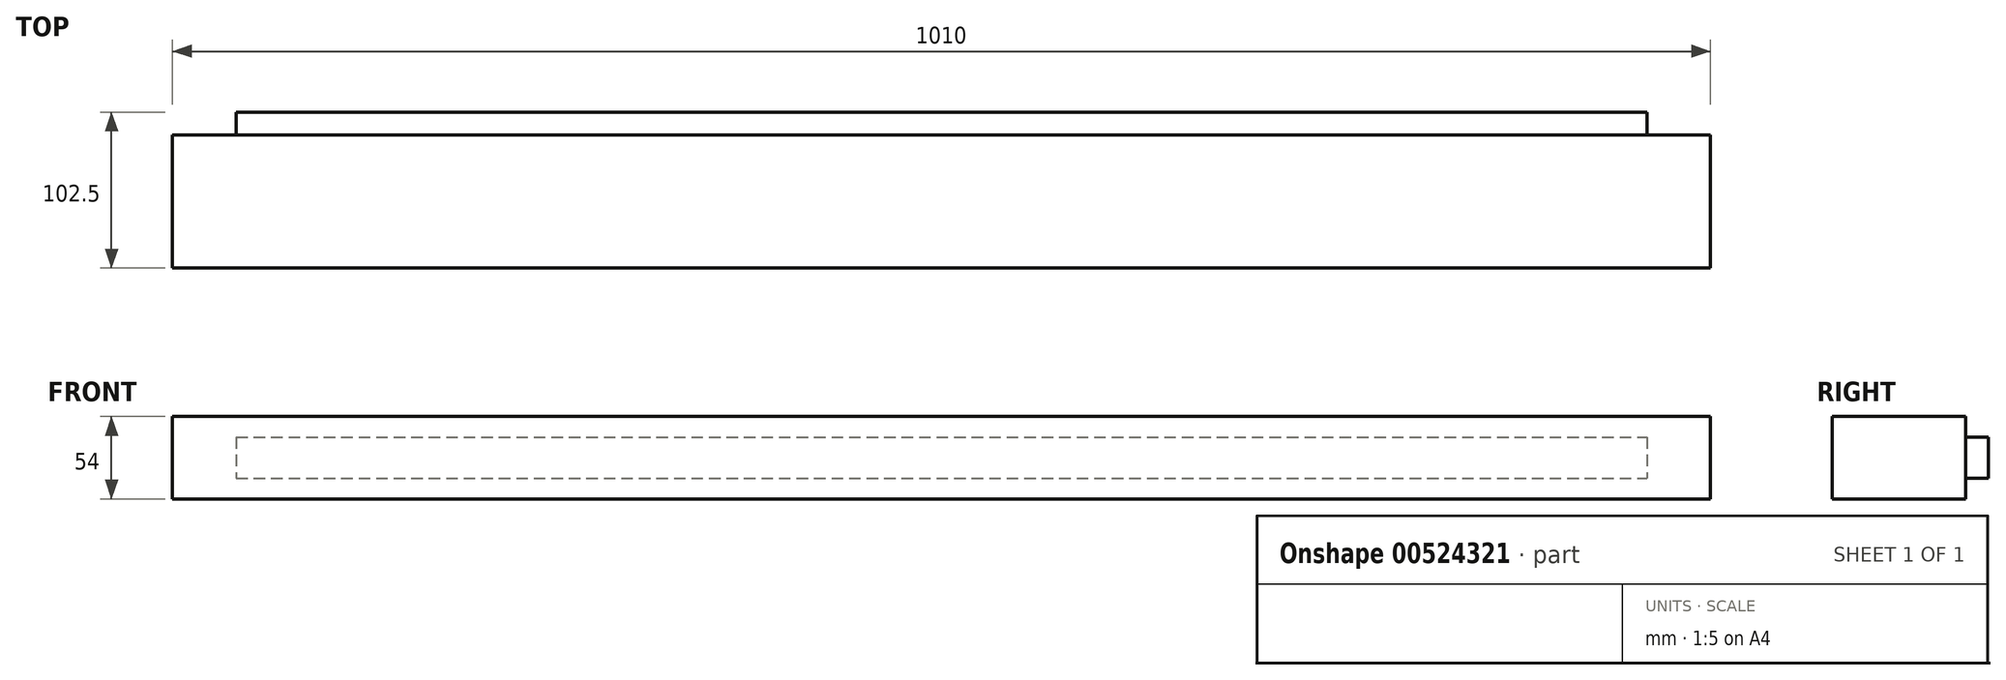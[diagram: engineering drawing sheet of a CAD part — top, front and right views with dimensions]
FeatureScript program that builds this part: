
annotation { "Feature Type Name" : "Feature", "Feature Type Description" : "" }
export const myFeature = defineFeature(function(context is Context, id is Id, definition is map)
    precondition{}
    {
        {
            var Q0;
            Q0=qCreatedBy(makeId("Front.planeOp"),FACE);
            var sketch = newSketch(context, id + "F0", { "sketchPlane" : qUnion([Q0])});
            skLineSegment(sketch, "E0.bottom", {"start": v(505, -27) * mm, "end": v(-505, -27) * mm});
            skLineSegment(sketch, "E0.top", {"start": v(505, 27) * mm, "end": v(-505, 27) * mm});
            skLineSegment(sketch, "E0.left", {"start": v(505, -27) * mm, "end": v(505, 27) * mm});
            skLineSegment(sketch, "E0.right", {"start": v(-505, -27) * mm, "end": v(-505, 27) * mm});
            skPoint(sketch, "E0.middle", {"position": v(0, 0) * mm});
            skSolve(sketch);
        }
        {
            var Q0;
            Q0=makeQuery(id+"F0.imprint","IMPRINT",FACE,{"disambiguationData":[TD([[makeQuery(id+"F0.imprint","IMPRINT",EDGE,{"derivedFrom":sQuery(id+"F0.wireOp",EDGE,"E0.bottom")}),-1.0]])]});
            extrude(context, id + "F1", {"entities" : qUnion([Q0]), "depth" : 87.5 * mm, "offsetDistance" : 25 * mm});
        }
        {
            var Q0;
            Q0=makeQuery(id+"F1.opExtrude","CAP_FACE",FACE,{"disambiguationData":[OSD([sQuery(id+"F0.wireOp",EDGE,"E0.bottom"),sQuery(id+"F0.wireOp",EDGE,"E0.top"),sQuery(id+"F0.wireOp",EDGE,"E0.left"),sQuery(id+"F0.wireOp",EDGE,"E0.right")])],"isStart":true});
            var sketch = newSketch(context, id + "F2", { "sketchPlane" : qUnion([Q0])});
            skLineSegment(sketch, "E1.bottom", {"start": v(463.18, 13.4) * mm, "end": v(-463.18, 13.4) * mm});
            skLineSegment(sketch, "E1.top", {"start": v(463.18, -13.4) * mm, "end": v(-463.18, -13.4) * mm});
            skLineSegment(sketch, "E1.left", {"start": v(463.18, 13.4) * mm, "end": v(463.18, -13.4) * mm});
            skLineSegment(sketch, "E1.right", {"start": v(-463.18, 13.4) * mm, "end": v(-463.18, -13.4) * mm});
            skPoint(sketch, "E1.middle", {"position": v(0, 0) * mm});
            skSolve(sketch);
        }
        {
            var Q0;
            Q0=makeQuery(id+"F2.imprint","IMPRINT",FACE,{"disambiguationData":[TD([[makeQuery(id+"F2.imprint","IMPRINT",EDGE,{"derivedFrom":sQuery(id+"F2.wireOp",EDGE,"E1.bottom")}),1.0]])]});
            extrude(context, id + "F3", {"entities" : qUnion([Q0]), "depth" : 15 * mm, "offsetDistance" : 25 * mm});
        }
    });
